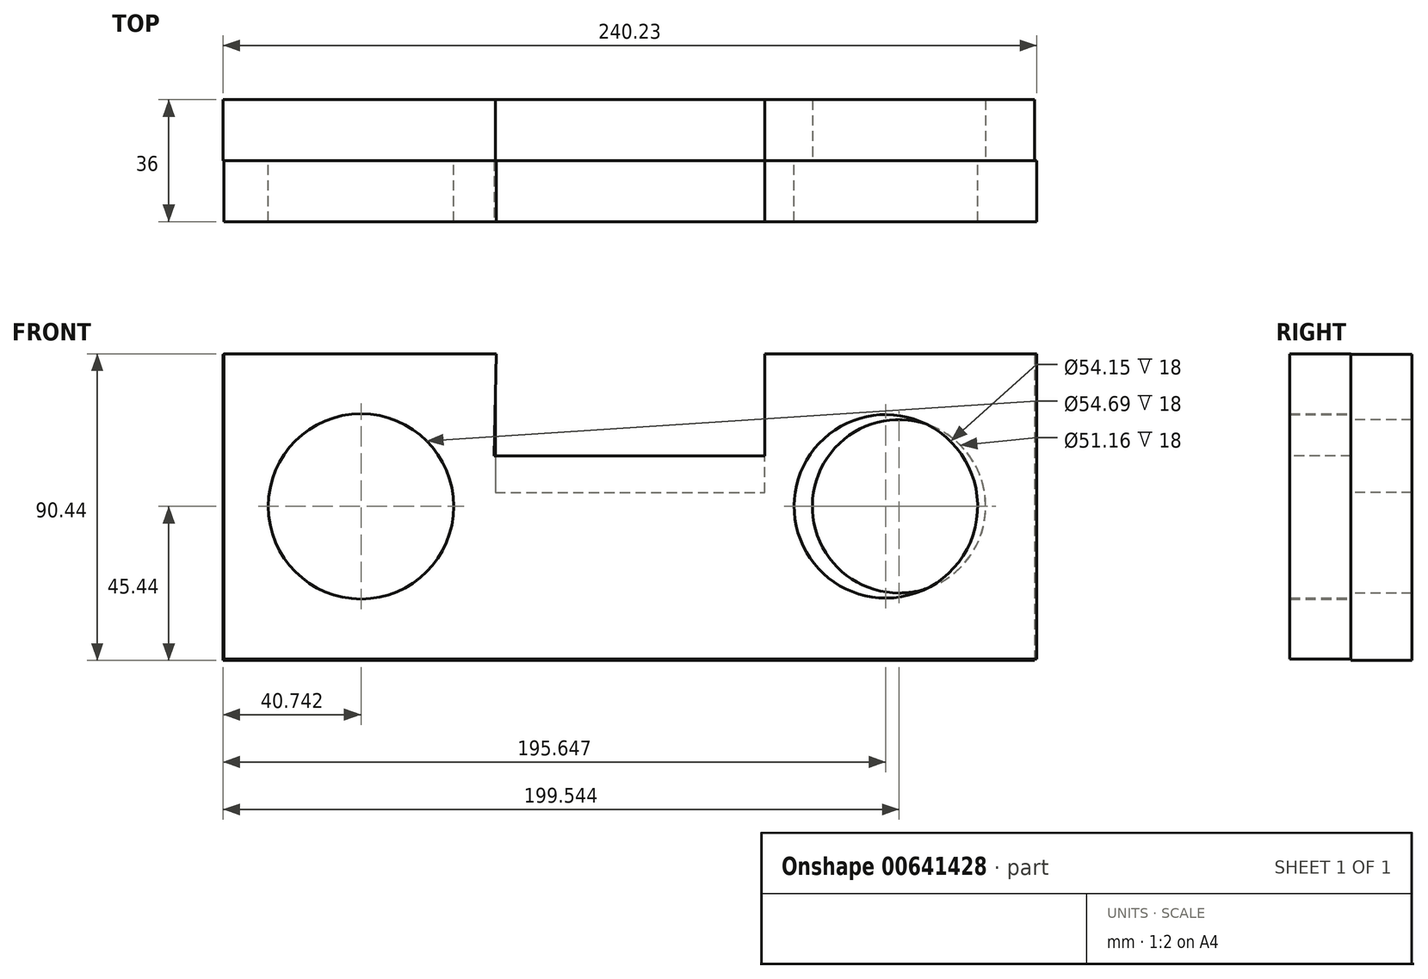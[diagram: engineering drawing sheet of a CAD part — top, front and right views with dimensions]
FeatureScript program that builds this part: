
annotation { "Feature Type Name" : "Feature", "Feature Type Description" : "" }
export const myFeature = defineFeature(function(context is Context, id is Id, definition is map)
    precondition{}
    {
        {
            var Q0;
            Q0=qCreatedBy(makeId("Front.planeOp"),FACE);
            var sketch = newSketch(context, id + "F0", { "sketchPlane" : qUnion([Q0])});
            skLineSegment(sketch, "E0.bottom", {"start": v(-120, -45) * mm, "end": v(120, -45) * mm});
            skLineSegment(sketch, "E0.top", {"start": v(-120, 45) * mm, "end": v(120, 45) * mm});
            skLineSegment(sketch, "E0.left", {"start": v(-120, -45) * mm, "end": v(-120, 45) * mm});
            skLineSegment(sketch, "E0.right", {"start": v(120, -45) * mm, "end": v(120, 45) * mm});
            skPoint(sketch, "E0.middle", {"position": v(0, 0) * mm});
            skLineSegment(sketch, "E1", {"start": v(-120, 2.16) * mm, "end": v(-40, 2.16) * mm});
            skLineSegment(sketch, "E2", {"start": v(120, 0) * mm, "end": v(40, 0) * mm});
            skPoint(sketch, "E2.endSnap0", {"position": v(120, 0) * mm});
            skLineSegment(sketch, "E3", {"start": v(-40, 45) * mm, "end": v(-40, -45) * mm});
            skLineSegment(sketch, "E4", {"start": v(40, 45) * mm, "end": v(40, -45) * mm});
            skSolve(sketch);
        }
        {
            var Q0;
            {var subQ0=sQuery(id+"F0.wireOp",EDGE,"E3");var subQ2=sQuery(id+"F0.wireOp",EDGE,"E0.bottom");var subQ3=makeQuery(id+"F0.imprint","INTERSECT",VERTEX,{"derivedFrom":[subQ2,subQ0]});Q0=makeQuery(id+"F0.imprint","IMPRINT",FACE,{"disambiguationData":[TD([[makeQuery(id+"F0.imprint","IMPRINT",EDGE,{"disambiguationData":[TD([[subQ3,-1.0]])],"derivedFrom":subQ2}),1.0]])]});}
            var sketch = newSketch(context, id + "F1", { "sketchPlane" : qUnion([Q0])});
            skLineSegment(sketch, "E5", {"start": v(-39.55, 45.2) * mm, "end": v(39.62, 45.2) * mm});
            skLineSegment(sketch, "E6", {"start": v(39.62, 45.2) * mm, "end": v(39.62, 14.88) * mm});
            skLineSegment(sketch, "E7", {"start": v(39.62, 14.88) * mm, "end": v(-40.22, 14.88) * mm});
            skLineSegment(sketch, "E8", {"start": v(-40.22, 14.88) * mm, "end": v(-39.55, 45.2) * mm});
            skSolve(sketch);
        }
        {
            var Q0;
            Q0 = qSketchRegion(id + "F1", true);
            var Q1;
            Q1 = qSketchRegion(id + "F0", true);
            extrude(context, id + "F2", {"entities" : qUnion([Q0, Q1]), "depth" : 18 * mm, "offsetDistance" : 25 * mm});
        }
        {
            var Q0;
            Q0=makeQuery(id+"F2.opExtrude","CAP_FACE",FACE,{"disambiguationData":[OSD([sQuery(id+"F1.wireOp",EDGE,"E5"),sQuery(id+"F1.wireOp",EDGE,"E6"),sQuery(id+"F1.wireOp",EDGE,"E7"),sQuery(id+"F1.wireOp",EDGE,"E8")])],"isStart":false});
            var sketch = newSketch(context, id + "F3", { "sketchPlane" : qUnion([Q0])});
            skSolve(sketch);
        }
        {
            var Q0;
            Q0=makeQuery(id+"F3.imprint","IMPRINT",FACE,{"disambiguationData":[TD([[makeQuery(id+"F3.imprint","IMPRINT",EDGE,{"derivedFrom":makeQuery(id+"F2.opExtrude","CAP_EDGE",EDGE,{"disambiguationData":[OSD([sQuery(id+"F1.wireOp",EDGE,"E5")])],"isStart":false})}),-1.0]])]});
            extrude(context, id + "F4", {"entities" : qUnion([Q0]), "operationType" : NewBodyOperationType.REMOVE, "oppositeDirection" : true, "depth" : 25 * mm, "offsetDistance" : 25 * mm});
        }
        {
            var Q0;
            Q0=qCreatedBy(makeId("Front.planeOp"),FACE);
            var sketch = newSketch(context, id + "F5", { "sketchPlane" : qUnion([Q0])});
            skCircle(sketch, "E9", {"center": v(-79.49, 0) * mm, "radius": 27.35 * mm});
            skPoint(sketch, "E10.center.orphan", {"position": v(75.42, 0) * mm});
            skCircle(sketch, "E11", {"center": v(75.42, 0) * mm, "radius": 27.08 * mm});
            skSolve(sketch);
        }
        {
            var Q0;
            Q0 = qSketchRegion(id + "F5", true);
            extrude(context, id + "F6", {"entities" : qUnion([Q0]), "operationType" : NewBodyOperationType.REMOVE, "depth" : 58.2 * mm, "offsetDistance" : 25 * mm});
        }
        {
            var Q0;
            Q0=qCreatedBy(makeId("Front.planeOp"),FACE);
            var sketch = newSketch(context, id + "F7", { "sketchPlane" : qUnion([Q0])});
            skLineSegment(sketch, "E12", {"start": v(119.36, 44.86) * mm, "end": v(119.36, -45.44) * mm});
            skLineSegment(sketch, "E13", {"start": v(119.36, -45.44) * mm, "end": v(-120.23, -45.44) * mm});
            skLineSegment(sketch, "E14", {"start": v(-120.23, -45.44) * mm, "end": v(-120.23, 44.9) * mm});
            skLineSegment(sketch, "E15", {"start": v(-120.23, 44.9) * mm, "end": v(-39.86, 44.9) * mm});
            skLineSegment(sketch, "E16", {"start": v(-39.86, 44.9) * mm, "end": v(-39.86, 4.03) * mm});
            skLineSegment(sketch, "E17", {"start": v(-39.86, 4.03) * mm, "end": v(39.65, 4.03) * mm});
            skLineSegment(sketch, "E18", {"start": v(39.65, 4.03) * mm, "end": v(39.65, 44.9) * mm});
            skLineSegment(sketch, "E19", {"start": v(39.65, 44.9) * mm, "end": v(119.36, 44.86) * mm});
            skSolve(sketch);
        }
        {
            var Q0;
            Q0 = qSketchRegion(id + "F7", true);
            var Q1;
            Q1 = qSketchRegion(id + "F9", true);
            extrude(context, id + "F8", {"entities" : qUnion([Q0, Q1]), "operationType" : NewBodyOperationType.ADD, "oppositeDirection" : true, "depth" : 18 * mm, "offsetDistance" : 25 * mm});
        }
        {
            var Q0;
            Q0=qCreatedBy(makeId("Front.planeOp"),FACE);
            var sketch = newSketch(context, id + "F9", { "sketchPlane" : qUnion([Q0])});
            skCircle(sketch, "E20", {"center": v(79.31, 0) * mm, "radius": 25.58 * mm});
            skPoint(sketch, "E21.end.orphan", {"position": v(79.31, -45.36) * mm});
            skPoint(sketch, "E22.orphan", {"position": v(119.32, -45.36) * mm});
            skPoint(sketch, "E23.end.orphan", {"position": v(39.3, -45.36) * mm});
            skSolve(sketch);
        }
        {
            var Q0;
            Q0 = qSketchRegion(id + "F9", true);
            extrude(context, id + "F10", {"entities" : qUnion([Q0]), "operationType" : NewBodyOperationType.REMOVE, "oppositeDirection" : true, "depth" : 63.8 * mm, "offsetDistance" : 25 * mm});
        }
    });
